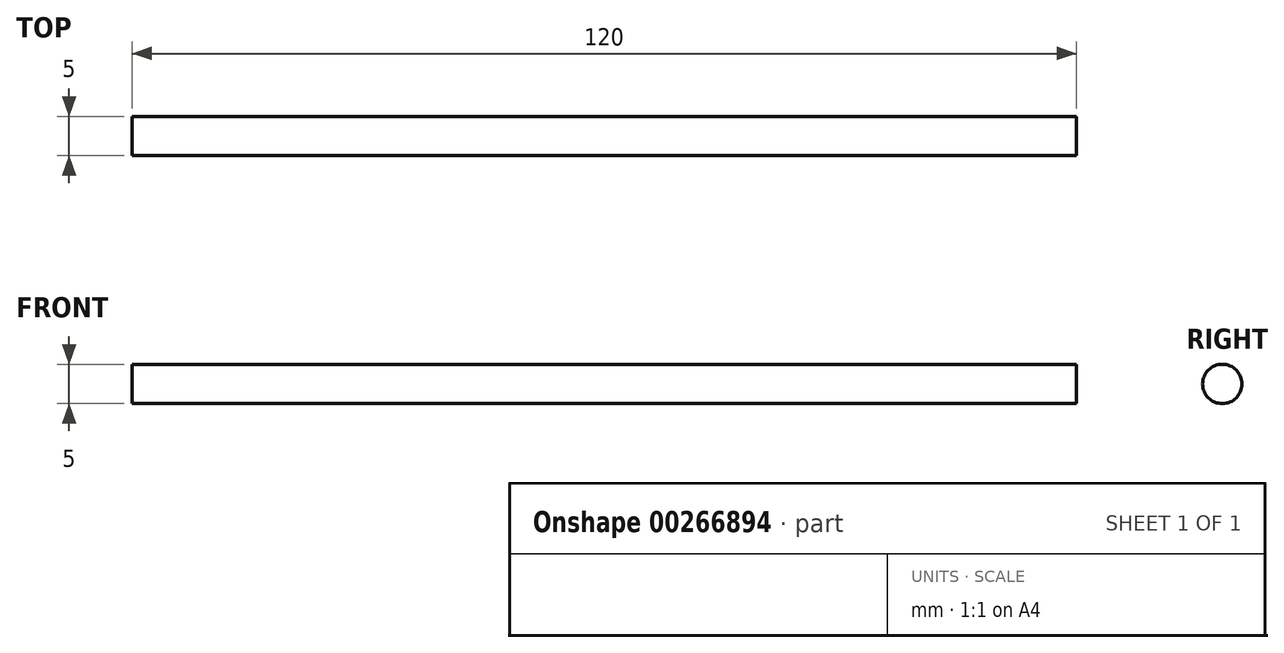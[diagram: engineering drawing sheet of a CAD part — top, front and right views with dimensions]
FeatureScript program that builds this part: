
annotation { "Feature Type Name" : "Feature", "Feature Type Description" : "" }
export const myFeature = defineFeature(function(context is Context, id is Id, definition is map)
    precondition{}
    {
        {
            var Q0;
            Q0=qCreatedBy(makeId("Right.planeOp"),FACE);
            var sketch = newSketch(context, id + "F0", { "sketchPlane" : qUnion([Q0])});
            skCircle(sketch, "E0", {"center": v(0, 0) * mm, "radius": 2.5 * mm});
            skSolve(sketch);
        }
        {
            var Q0;
            Q0 = qSketchRegion(id + "F0", true);
            extrude(context, id + "F1", {"entities" : qUnion([Q0]), "depth" : 60 * mm, "hasSecondDirection" : true, "secondDirectionOppositeDirection" : true, "secondDirectionDepth" : 60 * mm});
        }
    });
